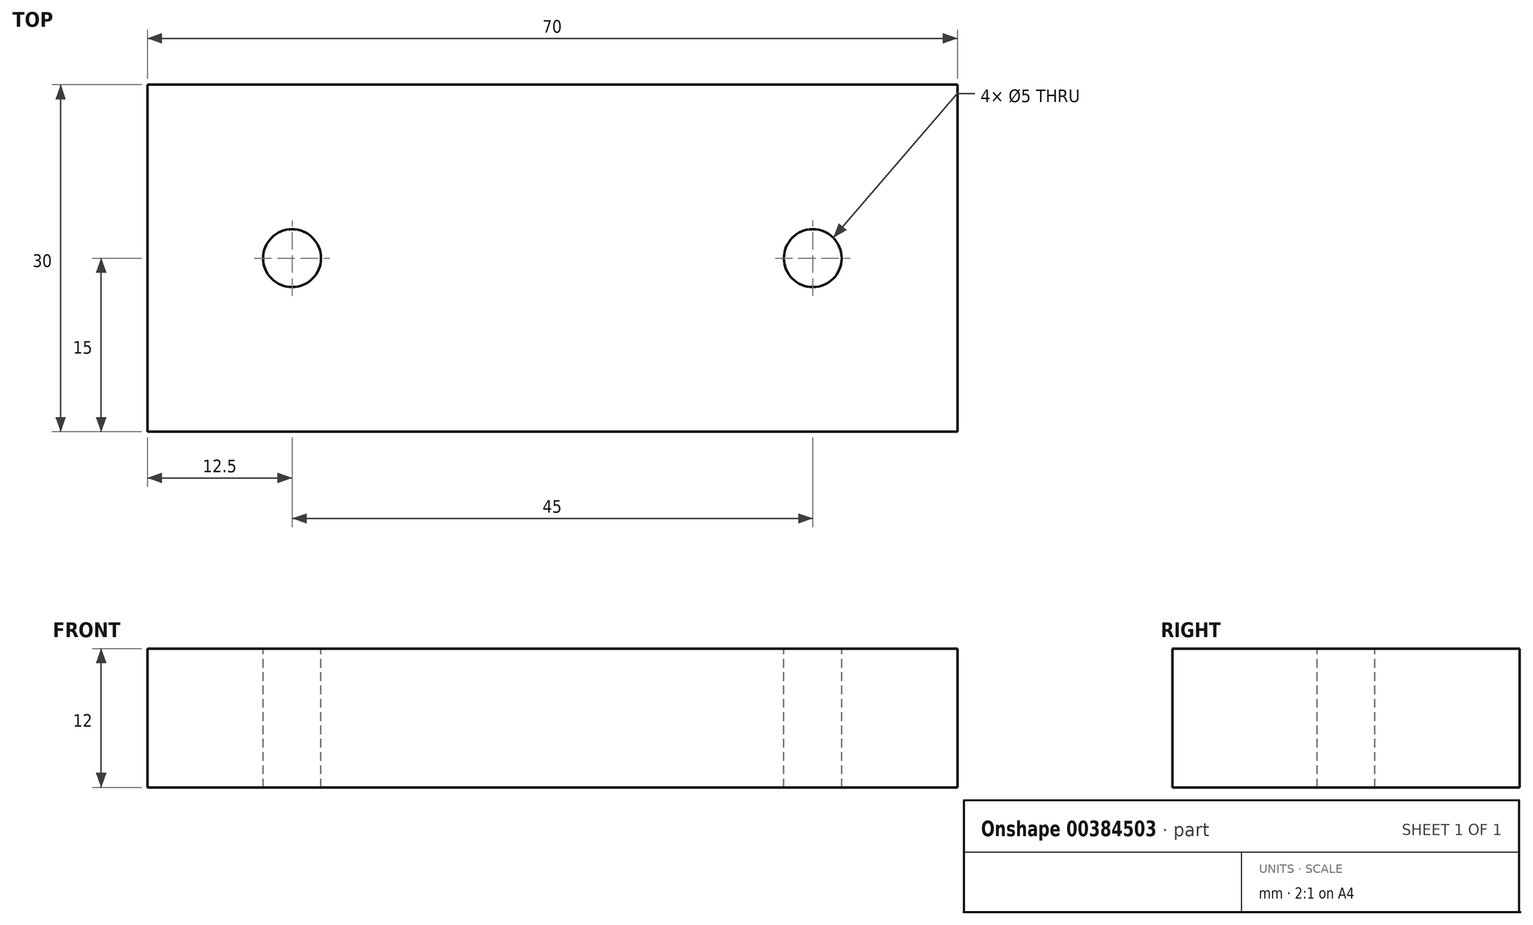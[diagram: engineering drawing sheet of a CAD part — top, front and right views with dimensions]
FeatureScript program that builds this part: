
annotation { "Feature Type Name" : "Feature", "Feature Type Description" : "" }
export const myFeature = defineFeature(function(context is Context, id is Id, definition is map)
    precondition{}
    {
        {
            var Q0;
            Q0=qCreatedBy(makeId("Top.planeOp"),FACE);
            var sketch = newSketch(context, id + "F0", { "sketchPlane" : qUnion([Q0])});
            skLineSegment(sketch, "E0.bottom", {"start": v(35, -15) * mm, "end": v(-35, -15) * mm});
            skLineSegment(sketch, "E0.top", {"start": v(35, 15) * mm, "end": v(-35, 15) * mm});
            skLineSegment(sketch, "E0.left", {"start": v(35, -15) * mm, "end": v(35, 15) * mm});
            skLineSegment(sketch, "E0.right", {"start": v(-35, -15) * mm, "end": v(-35, 15) * mm});
            skPoint(sketch, "E0.middle", {"position": v(0, 0) * mm});
            skSolve(sketch);
        }
        {
            var Q0;
            Q0=makeQuery(id+"F0.imprint","IMPRINT",FACE,{"disambiguationData":[TD([[makeQuery(id+"F0.imprint","IMPRINT",EDGE,{"derivedFrom":sQuery(id+"F0.wireOp",EDGE,"E0.bottom")}),-1.0]])]});
            extrude(context, id + "F1", {"entities" : qUnion([Q0]), "depth" : 12 * mm});
        }
        {
            var Q0;
            Q0=makeQuery(id+"F1.opExtrude","CAP_FACE",FACE,{"disambiguationData":[OSD([sQuery(id+"F0.wireOp",EDGE,"E0.bottom"),sQuery(id+"F0.wireOp",EDGE,"E0.top"),sQuery(id+"F0.wireOp",EDGE,"E0.left"),sQuery(id+"F0.wireOp",EDGE,"E0.right")])],"isStart":false});
            var sketch = newSketch(context, id + "F2", { "sketchPlane" : qUnion([Q0])});
            skLineSegment(sketch, "E1", {"start": v(-35, 0) * mm, "end": v(-22.5, 0) * mm, "construction": true});
            skLineSegment(sketch, "E2", {"start": v(-22.5, 0) * mm, "end": v(22.5, 0) * mm, "construction": true});
            skLineSegment(sketch, "E3", {"start": v(22.5, 0) * mm, "end": v(35, 0) * mm, "construction": true});
            skSolve(sketch);
        }
        {
            var Q0;
            Q0=sQuery(id+"F2.wireOp",VERTEX,"E2.start");
            var Q1;
            Q1=sQuery(id+"F2.wireOp",VERTEX,"E3.start");
            var Q2;
            Q2=makeQuery(id+"F1.opExtrude","SWEPT_BODY",BODY,{"disambiguationData":[OSD([sQuery(id+"F0.wireOp",EDGE,"E0.bottom"),sQuery(id+"F0.wireOp",EDGE,"E0.top"),sQuery(id+"F0.wireOp",EDGE,"E0.left"),sQuery(id+"F0.wireOp",EDGE,"E0.right")])]});
            hole(context, id + "F3", {"style" : HoleStyle.SIMPLE, "endStyle" : HoleEndStyle.BLIND, "holeDiameter" : 5 * mm, "holeDepth" : 25 * mm, "isTappedThrough" : true, "tappedDepth" : 12 * mm, "tapClearance" : 3, "locations" : qUnion([Q0, Q1]), "scope" : qUnion([Q2])});
        }
    });
